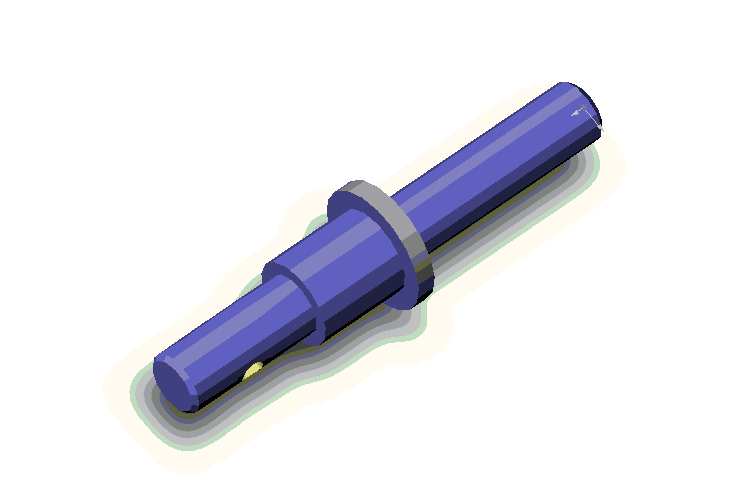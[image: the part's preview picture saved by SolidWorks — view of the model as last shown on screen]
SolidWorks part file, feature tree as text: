
SOLIDWORKS PART (.sldprt)
format: sldprt  version: not decoded by parser v0  size: 81,920 bytes
history: native  units: mm
features: plane x3, sketch x2, chamfer x2, revolve x1, cut_extrude x1 (+5 scaffold rows collapsed)
feature tree (14):
  scaffold x5  (default folders/planes/origin — collapsed)
  plane  "Plan1"
  plane  "Plan2"
  plane  "Plan3"
  sketch  "Esquisse3"  dims[D1=5.0mm D2=0.75mm D3=5.0mm D4=2.0mm D5=3.0mm D6=5.75mm D7=23.0mm D8=15.0mm D9=3.0mm D10=2.0mm D11=35.0mm]
  revolve  "Base-Révolution"  Angle=360deg
  chamfer  "Chanfrein1"  Distance=0.75mm Angle=45deg
  chamfer  "Chanfrein2"  Distance=1mm Angle=45deg
  sketch  "Esquisse4"  dims[D1=4.0mm D2=12.0mm]
  cut_extrude  "Enlèv. mat.-Extru.4"  Depth=10mm
decode coverage: 6 of 6 modeling features carry decoded parameters
note: suppression state not decoded; provenance and decode notes live in map.json
